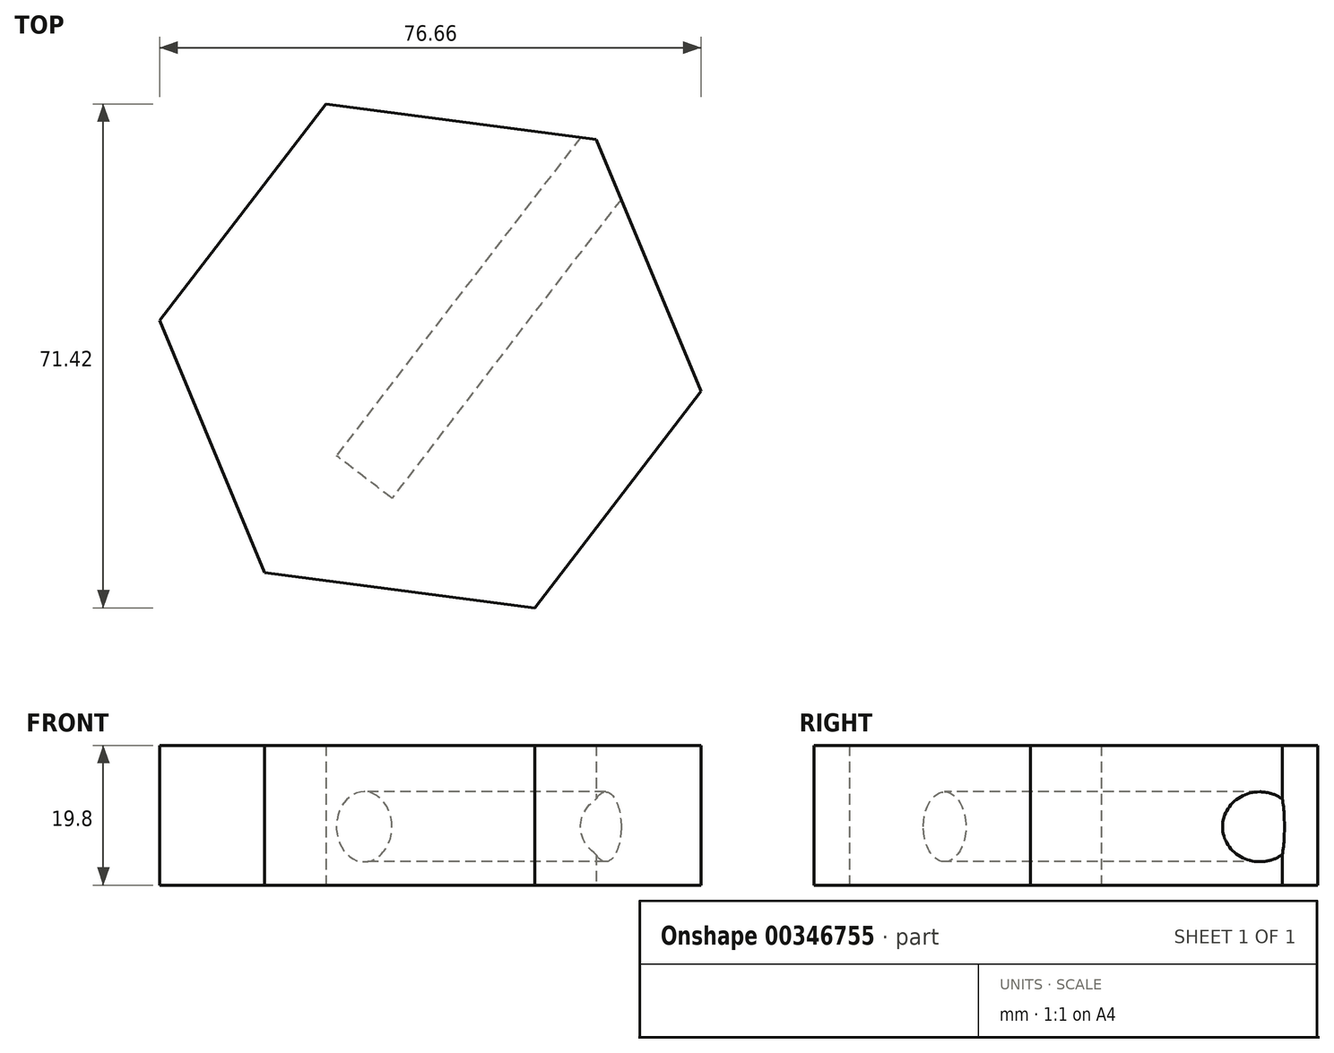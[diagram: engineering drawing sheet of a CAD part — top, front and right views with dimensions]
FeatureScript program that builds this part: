
annotation { "Feature Type Name" : "Feature", "Feature Type Description" : "" }
export const myFeature = defineFeature(function(context is Context, id is Id, definition is map)
    precondition{}
    {
        {
            var Q0;
            Q0=qCreatedBy(makeId("Top.planeOp"),FACE);
            var sketch = newSketch(context, id + "F0", { "sketchPlane" : qUnion([Q0])});
            skCircle(sketch, "E0.cCircle", {"center": v(0, 0) * mm, "radius": 33.48 * mm, "construction": true});
            skLineSegment(sketch, "E0.0", {"start": v(-38.33, 5.02) * mm, "end": v(-14.81, 35.7) * mm});
            skLineSegment(sketch, "E0.1", {"start": v(-14.81, 35.7) * mm, "end": v(23.52, 30.68) * mm});
            skLineSegment(sketch, "E0.2", {"start": v(23.52, 30.68) * mm, "end": v(38.33, -5.02) * mm});
            skLineSegment(sketch, "E0.3", {"start": v(38.33, -5.02) * mm, "end": v(14.81, -35.7) * mm});
            skLineSegment(sketch, "E0.4", {"start": v(14.81, -35.7) * mm, "end": v(-23.52, -30.68) * mm});
            skLineSegment(sketch, "E0.5", {"start": v(-23.52, -30.68) * mm, "end": v(-38.33, 5.02) * mm});
            skPoint(sketch, "E0.0.midPoint", {"position": v(-26.57, 20.37) * mm});
            skSolve(sketch);
        }
        {
            var Q0;
            Q0=makeQuery(id+"F0.imprint","IMPRINT",FACE,{"disambiguationData":[TD([[makeQuery(id+"F0.imprint","IMPRINT",EDGE,{"derivedFrom":sQuery(id+"F0.wireOp",EDGE,"E0.0")}),-1.0]])]});
            extrude(context, id + "F1", {"entities" : qUnion([Q0]), "depth" : 19.8 * mm});
        }
        {
            var Q0;
            Q0=makeQuery(id+"F1.opExtrude","CAP_VERTEX",VERTEX,{"disambiguationData":[OSD([sQuery(id+"F0.wireOp",EDGE,"E0.3"),sQuery(id+"F0.wireOp",EDGE,"E0.4")])],"isStart":false});
            var Q1;
            Q1=makeQuery(id+"F1.opExtrude","CAP_VERTEX",VERTEX,{"disambiguationData":[OSD([sQuery(id+"F0.wireOp",EDGE,"E0.3"),sQuery(id+"F0.wireOp",EDGE,"E0.4")])],"isStart":true});
            var Q2;
            Q2=makeQuery(id+"F1.opExtrude","CAP_VERTEX",VERTEX,{"disambiguationData":[OSD([sQuery(id+"F0.wireOp",EDGE,"E0.0"),sQuery(id+"F0.wireOp",EDGE,"E0.5")])],"isStart":false});
            cPlane(context, id + "F2", {"entities" : qUnion([Q0, Q1, Q2]), "cplaneType" : CPlaneType.THREE_POINT, "offset" : 25 * mm, "width" : 150 * mm, "height" : 150 * mm});
        }
        {
            var Q0;
            Q0=qCreatedBy(id+"F2.planeOp",FACE);
            var sketch = newSketch(context, id + "F3", { "sketchPlane" : qUnion([Q0])});
            skCircle(sketch, "E1", {"center": v(3, 8.27) * mm, "radius": 4.95 * mm});
            skSolve(sketch);
        }
        {
            var Q0;
            Q0 = qSketchRegion(id + "F3", true);
            extrude(context, id + "F4", {"entities" : qUnion([Q0]), "operationType" : NewBodyOperationType.REMOVE, "oppositeDirection" : true, "depth" : 65.3 * mm});
        }
    });
